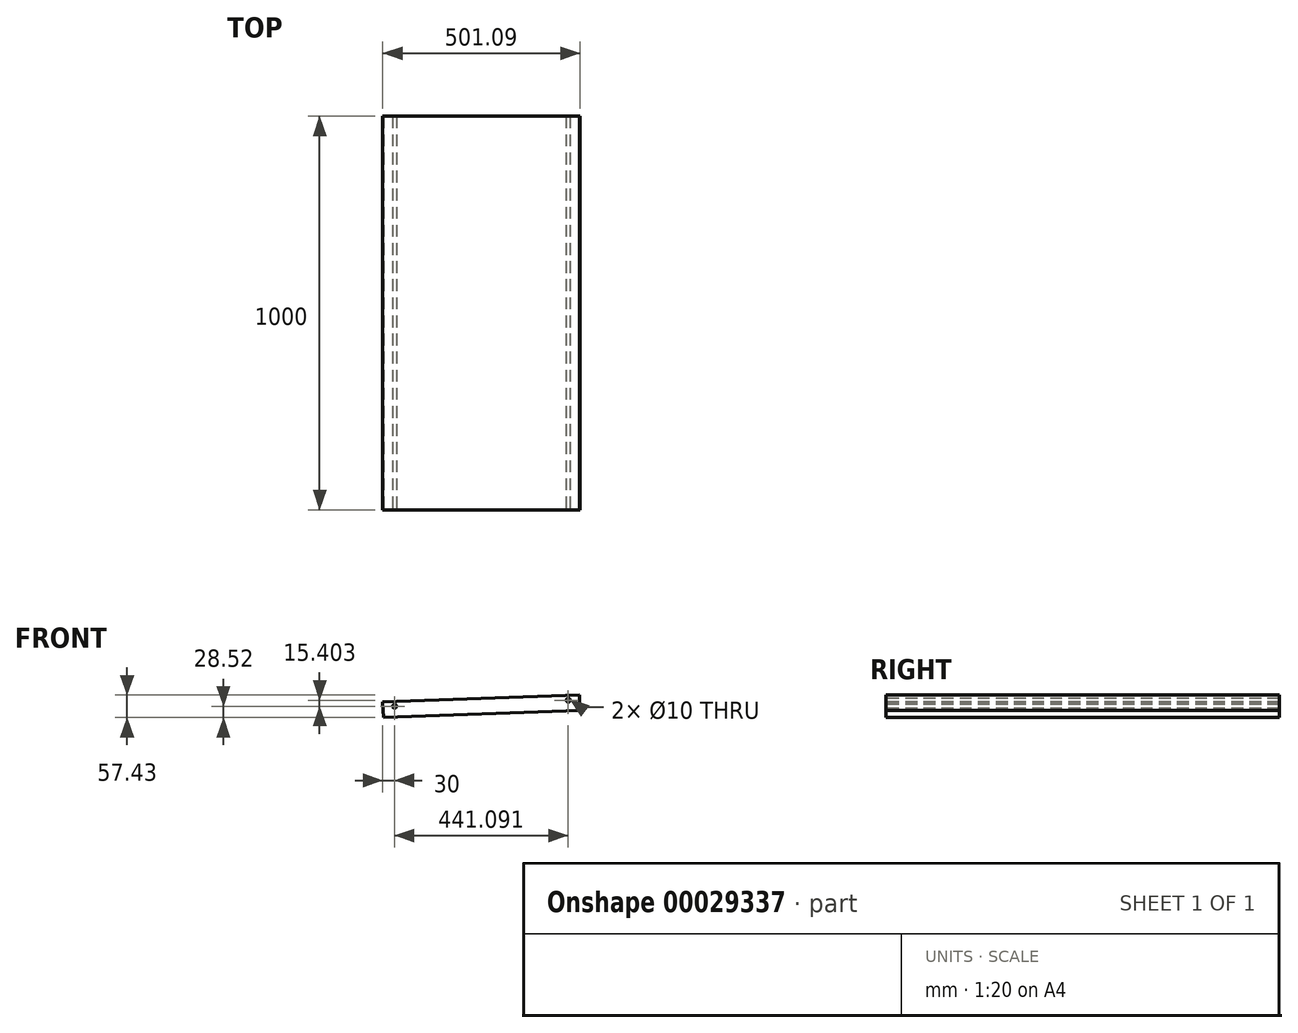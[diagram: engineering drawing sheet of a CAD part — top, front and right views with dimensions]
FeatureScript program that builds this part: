
annotation { "Feature Type Name" : "Feature", "Feature Type Description" : "" }
export const myFeature = defineFeature(function(context is Context, id is Id, definition is map)
    precondition{}
    {
        {
            var Q0;
            Q0=qCreatedBy(makeId("Front.planeOp"),FACE);
            var sketch = newSketch(context, id + "F0", { "sketchPlane" : qUnion([Q0])});
            skLineSegment(sketch, "E0", {"start": v(0, 0) * mm, "end": v(499.7, 17.45) * mm});
            skLineSegment(sketch, "E1", {"start": v(499.7, 17.45) * mm, "end": v(501.1, -22.53) * mm});
            skLineSegment(sketch, "E2", {"start": v(501.1, -22.53) * mm, "end": v(1.4, -39.98) * mm});
            skLineSegment(sketch, "E3", {"start": v(1.4, -39.98) * mm, "end": v(0, 0) * mm});
            skSolve(sketch);
        }
        {
            var Q0;
            Q0=makeQuery(id+"F0.imprint","IMPRINT",FACE,{"disambiguationData":[TD([[makeQuery(id+"F0.imprint","IMPRINT",EDGE,{"derivedFrom":sQuery(id+"F0.wireOp",EDGE,"E0")}),-1.0]])]});
            extrude(context, id + "F1", {"entities" : qUnion([Q0]), "oppositeDirection" : true, "depth" : 1000 * mm});
        }
        {
            var Q0;
            Q0=makeQuery(id+"F1.opExtrude","CAP_FACE",FACE,{"disambiguationData":[OSD([sQuery(id+"F0.wireOp",EDGE,"E0"),sQuery(id+"F0.wireOp",EDGE,"E1"),sQuery(id+"F0.wireOp",EDGE,"E2"),sQuery(id+"F0.wireOp",EDGE,"E3")])],"isStart":true});
            var sketch = newSketch(context, id + "F2", { "sketchPlane" : qUnion([Q0])});
            skPoint(sketch, "E4", {"position": v(471.1, 3.94) * mm});
            skPoint(sketch, "E5", {"position": v(30, -11.46) * mm});
            skSolve(sketch);
        }
        {
            var Q0;
            Q0=sQuery(id+"F2.wireOp",VERTEX,"E5");
            var Q1;
            Q1=sQuery(id+"F2.wireOp",VERTEX,"E4");
            var Q2;
            Q2=makeQuery(id+"F1.opExtrude","SWEPT_BODY",BODY,{"disambiguationData":[OSD([sQuery(id+"F0.wireOp",EDGE,"E0"),sQuery(id+"F0.wireOp",EDGE,"E1"),sQuery(id+"F0.wireOp",EDGE,"E2"),sQuery(id+"F0.wireOp",EDGE,"E3")])]});
            hole(context, id + "F3", {"style" : HoleStyle.SIMPLE, "holeDiameter" : 10 * mm, "endStyle" : HoleEndStyle.THROUGH, "locations" : qUnion([Q0, Q1]), "scope" : qUnion([Q2])});
        }
    });
